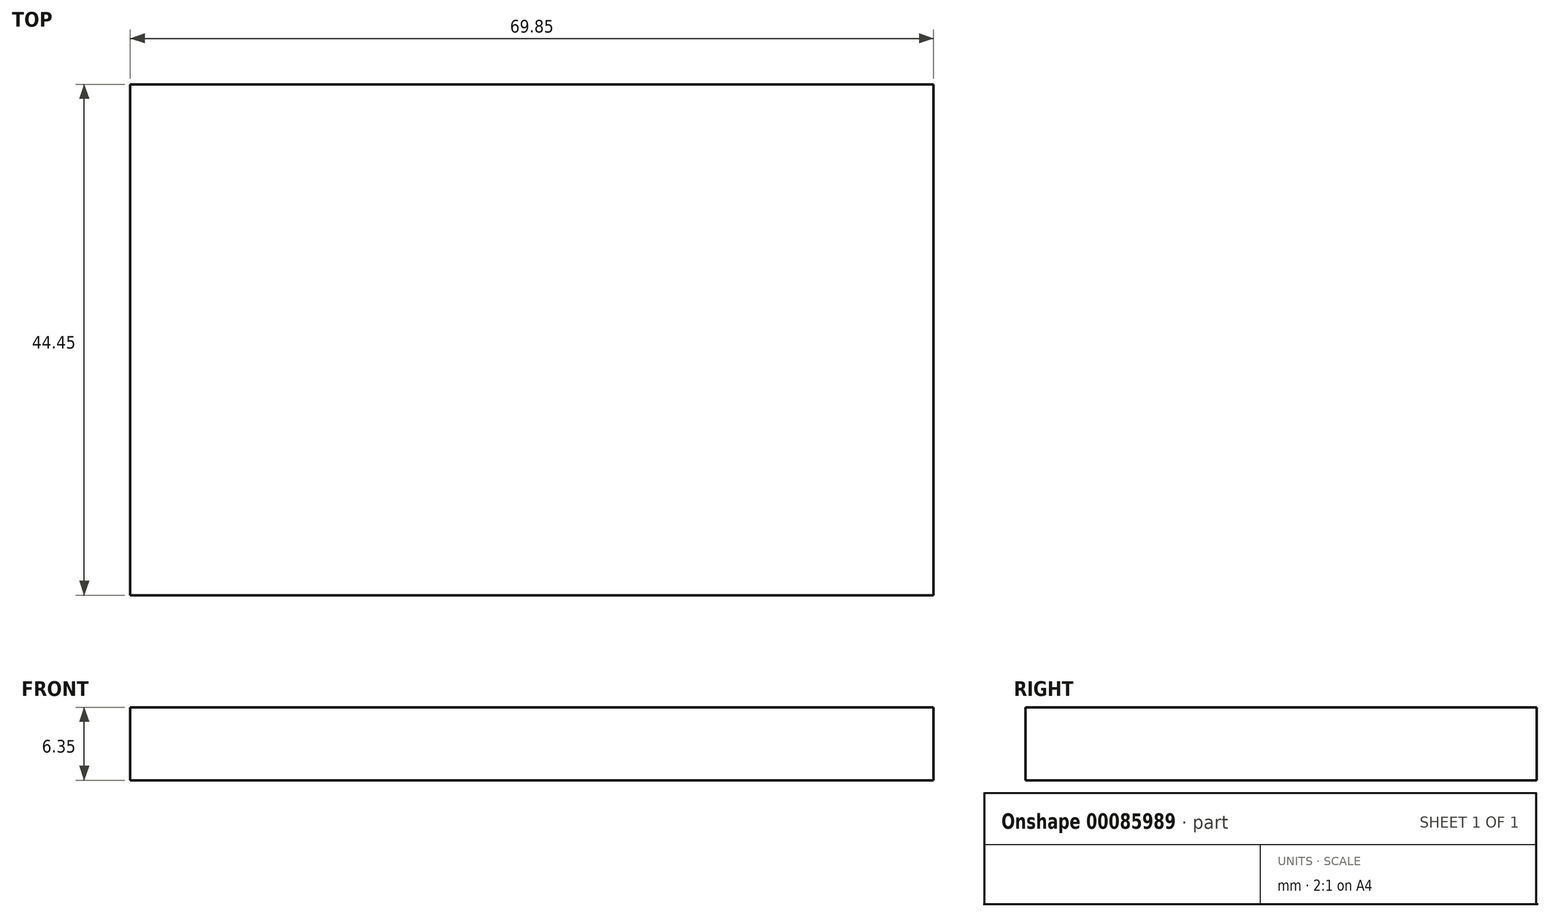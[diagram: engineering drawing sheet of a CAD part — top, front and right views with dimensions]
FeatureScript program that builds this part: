
annotation { "Feature Type Name" : "Feature", "Feature Type Description" : "" }
export const myFeature = defineFeature(function(context is Context, id is Id, definition is map)
    precondition{}
    {
        {
            var Q0;
            Q0=qCreatedBy(makeId("Top.planeOp"),FACE);
            var sketch = newSketch(context, id + "F0", { "sketchPlane" : qUnion([Q0])});
            skLineSegment(sketch, "E0.bottom", {"start": v(-37.65, 0) * mm, "end": v(32.2, 0) * mm});
            skLineSegment(sketch, "E0.top", {"start": v(-37.65, 44.45) * mm, "end": v(32.2, 44.45) * mm});
            skLineSegment(sketch, "E0.left", {"start": v(-37.65, 0) * mm, "end": v(-37.65, 44.45) * mm});
            skLineSegment(sketch, "E0.right", {"start": v(32.2, 0) * mm, "end": v(32.2, 44.45) * mm});
            skSolve(sketch);
        }
        {
            var Q0;
            Q0=makeQuery(id+"F0.imprint","IMPRINT",FACE,{"disambiguationData":[TD([[makeQuery(id+"F0.imprint","IMPRINT",EDGE,{"derivedFrom":sQuery(id+"F0.wireOp",EDGE,"E0.bottom")}),1.0]])]});
            extrude(context, id + "F1", {"entities" : qUnion([Q0]), "depth" : 6.35 * mm});
        }
    });
